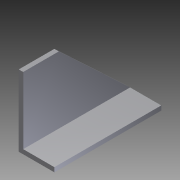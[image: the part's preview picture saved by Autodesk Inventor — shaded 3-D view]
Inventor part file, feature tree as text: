
AUTODESK INVENTOR PART (.ipt)
format: ipt  version: 2012 (Build 160160000, 160)  size: 83,456 bytes
history: native  units: in
note: dims shown in document units (in); Inventor stores cm internally (conversion verified against a paired STEP export)
features: extrude x2, sketch x2
ambient origin geometry x8: Origin, YZ Plane, XZ Plane, XY Plane, X Axis, Y Axis, Z Axis, Center Point
bodies: Solid1 (feature_tree)
feature tree (4):
  extrude  "Extrusion1"  Depth=1.0in
  extrude  "Extrusion2"  Depth=3.0in TaperAngle=0.0deg
  sketch  "Sketch1"  dims[d0=2.0in d1=1.0in]
  sketch  "Sketch2"  dims[d2=0.125in d3=3.0in d4=0.0in d5=1.0in d6=0.125in d7=1.0in d8=0.0in]
